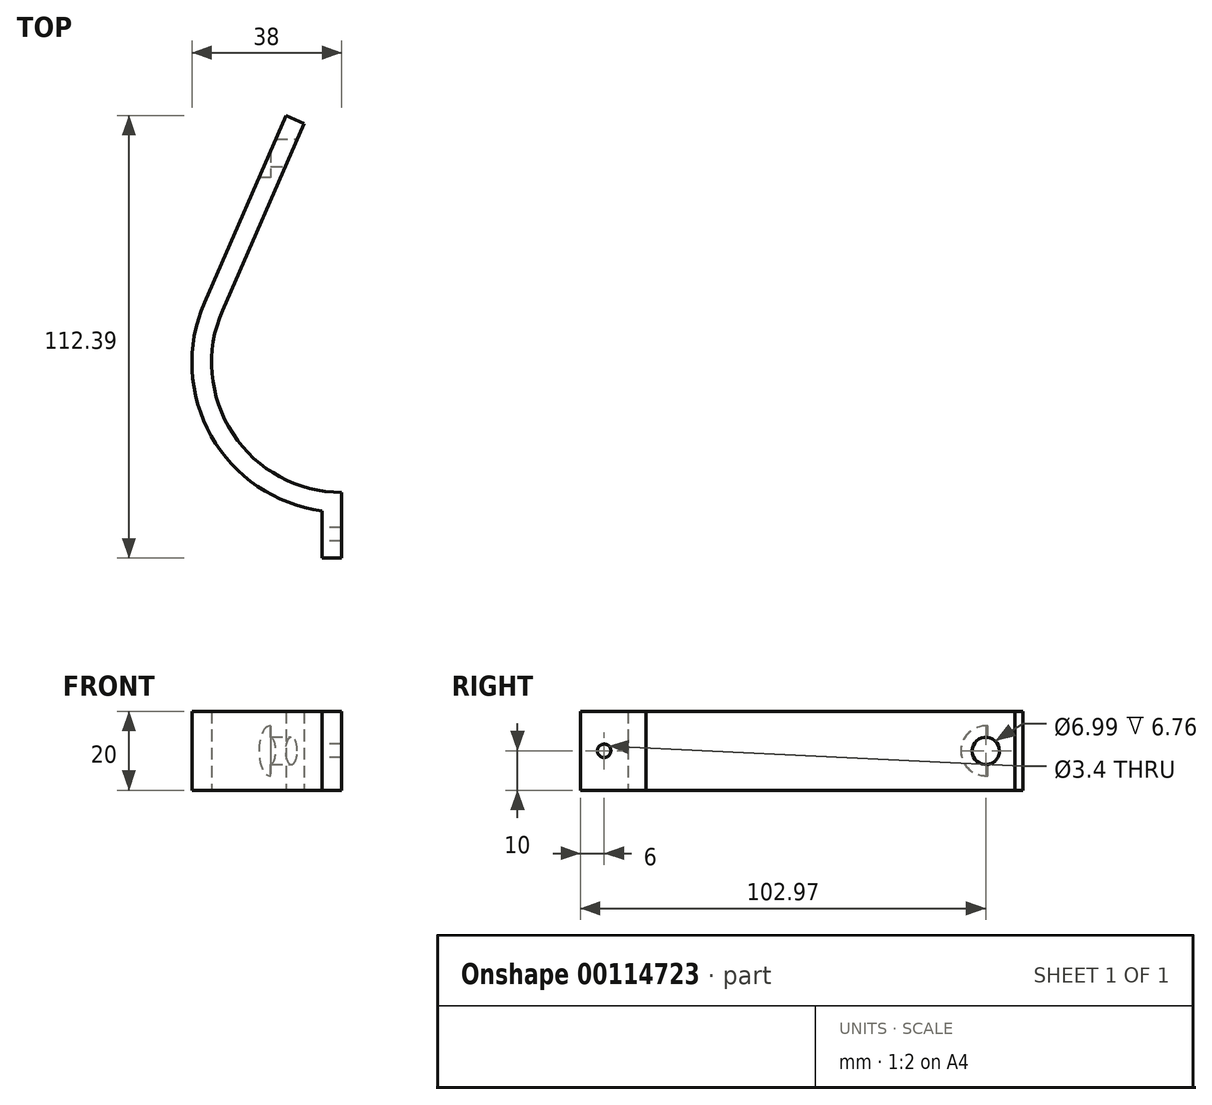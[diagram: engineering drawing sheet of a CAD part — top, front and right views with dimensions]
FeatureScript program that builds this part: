
annotation { "Feature Type Name" : "Feature", "Feature Type Description" : "" }
export const myFeature = defineFeature(function(context is Context, id is Id, definition is map)
    precondition{}
    {
        {
            var Q0;
            Q0=qCreatedBy(makeId("Top.planeOp"),FACE);
            var sketch = newSketch(context, id + "F0", { "sketchPlane" : qUnion([Q0])});
            skPoint(sketch, "E0", {"position": v(0, 98) * mm});
            skArc(sketch, "E1", {"start": v(10.73, 90.98) * mm, "mid": v(0, 98) * mm, "end": v(-10.73, 90.98) * mm});
            skArc(sketch, "E2", {"start": v(-30.25, 46.19) * mm, "mid": v(0, 0) * mm, "end": v(30.25, 46.19) * mm});
            skLineSegment(sketch, "E3", {"start": v(-10.73, 90.98) * mm, "end": v(-30.25, 46.19) * mm});
            skLineSegment(sketch, "E4", {"start": v(10.73, 90.98) * mm, "end": v(30.25, 46.19) * mm});
            skLineSegment(sketch, "E5.0", {"start": v(-15.3, 92.97) * mm, "end": v(-34.83, 48.19) * mm});
            skArc(sketch, "E5.1", {"start": v(15.3, 92.97) * mm, "mid": v(0, 103) * mm, "end": v(-15.3, 92.97) * mm});
            skLineSegment(sketch, "E5.2", {"start": v(15.3, 92.97) * mm, "end": v(34.83, 48.19) * mm});
            skArc(sketch, "E5.3", {"start": v(-34.83, 48.19) * mm, "mid": v(-33.1, 14.32) * mm, "end": v(-5, -4.67) * mm});
            skLineSegment(sketch, "E6", {"start": v(-5, -4.67) * mm, "end": v(-5, -16.67) * mm});
            skLineSegment(sketch, "E7", {"start": v(-5, -16.67) * mm, "end": v(0, -16.67) * mm});
            skArc(sketch, "E8.trimOffspring", {"start": v(0, -5) * mm, "mid": v(31.79, 12.18) * mm, "end": v(34.83, 48.19) * mm});
            skLineSegment(sketch, "E9", {"start": v(0, -5) * mm, "end": v(0, -16.67) * mm});
            skCircle(sketch, "E10", {"center": v(0, 86.3) * mm, "radius": 11.7 * mm, "construction": true});
            skSolve(sketch);
        }
        {
            var Q0;
            Q0=makeQuery(id+"F0.imprint","IMPRINT",FACE,{"disambiguationData":[TD([[makeQuery(id+"F0.imprint","IMPRINT",EDGE,{"derivedFrom":sQuery(id+"F0.wireOp",EDGE,"E1")}),-1.0]])]});
            extrude(context, id + "F1", {"entities" : qUnion([Q0]), "depth" : 20 * mm});
        }
        {
            var Q0;
            Q0=qCreatedBy(makeId("Right.planeOp"),FACE);
            var sketch = newSketch(context, id + "F2", { "sketchPlane" : qUnion([Q0])});
            skPoint(sketch, "E11.0", {"position": v(86.3, 0) * mm});
            skLineSegment(sketch, "E12", {"start": v(86.3, 0) * mm, "end": v(86.3, 10) * mm, "construction": true});
            skCircle(sketch, "E13", {"center": v(86.3, 10) * mm, "radius": 3.5 * mm});
            skSolve(sketch);
        }
        {
            var Q0;
            Q0=makeQuery(id+"F2.imprint","IMPRINT",FACE,{"disambiguationData":[TD([[makeQuery(id+"F2.imprint","IMPRINT",EDGE,{"derivedFrom":sQuery(id+"F2.wireOp",EDGE,"E13")}),1.0]])]});
            extrude(context, id + "F3", {"entities" : qUnion([Q0]), "operationType" : NewBodyOperationType.REMOVE, "endBound" : BoundingType.SYMMETRIC, "oppositeDirection" : true, "depth" : 100 * mm});
        }
        {
            var Q0;
            Q0=qCreatedBy(makeId("Right.planeOp"),FACE);
            cPlane(context, id + "F4", {"entities" : qUnion([Q0]), "cplaneType" : CPlaneType.OFFSET, "offset" : 25 * mm, "oppositeDirection" : true, "width" : 150 * mm, "height" : 150 * mm});
        }
        {
            var Q0;
            Q0=qCreatedBy(id+"F4.planeOp",FACE);
            var sketch = newSketch(context, id + "F5", { "sketchPlane" : qUnion([Q0])});
            skCircle(sketch, "E14.0", {"center": v(86.3, 10) * mm, "radius": 3.5 * mm});
            skCircle(sketch, "E15", {"center": v(86.3, 10) * mm, "radius": 6.35 * mm});
            skSolve(sketch);
        }
        {
            var Q0;
            Q0 = qSketchRegion(id + "F5", true);
            extrude(context, id + "F6", {"entities" : qUnion([Q0]), "operationType" : NewBodyOperationType.REMOVE, "depth" : 7 * mm});
        }
        {
            var Q0;
            Q0=makeQuery(id+"F1.opExtrude","CAP_FACE",FACE,{"disambiguationData":[OSD([sQuery(id+"F0.wireOp",EDGE,"E1"),sQuery(id+"F0.wireOp",EDGE,"E2"),sQuery(id+"F0.wireOp",EDGE,"E3"),sQuery(id+"F0.wireOp",EDGE,"E4"),sQuery(id+"F0.wireOp",EDGE,"E5.0"),sQuery(id+"F0.wireOp",EDGE,"E5.1"),sQuery(id+"F0.wireOp",EDGE,"E5.2"),sQuery(id+"F0.wireOp",EDGE,"E5.3"),sQuery(id+"F0.wireOp",EDGE,"E6"),sQuery(id+"F0.wireOp",EDGE,"E7"),sQuery(id+"F0.wireOp",EDGE,"E8.trimOffspring"),sQuery(id+"F0.wireOp",EDGE,"E9")])],"isStart":false});
            var sketch = newSketch(context, id + "F7", { "sketchPlane" : qUnion([Q0])});
            skPoint(sketch, "E16.firstSnap0", {"position": v(0, 103) * mm});
            skLineSegment(sketch, "E16.bottom", {"start": v(0, -28.68) * mm, "end": v(56.6, -28.68) * mm});
            skLineSegment(sketch, "E16.top", {"start": v(0, 106.36) * mm, "end": v(56.6, 106.36) * mm});
            skLineSegment(sketch, "E16.left", {"start": v(0, -28.68) * mm, "end": v(0, 106.36) * mm});
            skLineSegment(sketch, "E16.right", {"start": v(56.6, -28.68) * mm, "end": v(56.6, 106.36) * mm});
            skSolve(sketch);
        }
        {
            var Q0;
            Q0 = qSketchRegion(id + "F7", true);
            extrude(context, id + "F8", {"entities" : qUnion([Q0]), "operationType" : NewBodyOperationType.REMOVE, "oppositeDirection" : true, "depth" : 25 * mm});
        }
        {
            var Q0;
            Q0=makeQuery(id+"F1.opExtrude","SWEPT_FACE",FACE,{"disambiguationData":[OSD([sQuery(id+"F0.wireOp",EDGE,"E6")])]});
            var sketch = newSketch(context, id + "F9", { "sketchPlane" : qUnion([Q0])});
            skLineSegment(sketch, "E17", {"start": v(10.67, 20) * mm, "end": v(10.67, 0) * mm, "construction": true});
            skCircle(sketch, "E18", {"center": v(10.67, 10) * mm, "radius": 1.7 * mm});
            skSolve(sketch);
        }
        {
            var Q0;
            Q0=makeQuery(id+"F9.imprint","IMPRINT",FACE,{"disambiguationData":[TD([[makeQuery(id+"F9.imprint","IMPRINT",EDGE,{"derivedFrom":sQuery(id+"F9.wireOp",EDGE,"E18")}),1.0]])]});
            extrude(context, id + "F10", {"entities" : qUnion([Q0]), "operationType" : NewBodyOperationType.REMOVE, "oppositeDirection" : true, "depth" : 25 * mm});
        }
        {
            var Q0;
            Q0=makeQuery(id+"F1.opExtrude","CAP_FACE",FACE,{"disambiguationData":[OSD([sQuery(id+"F0.wireOp",EDGE,"E1"),sQuery(id+"F0.wireOp",EDGE,"E2"),sQuery(id+"F0.wireOp",EDGE,"E3"),sQuery(id+"F0.wireOp",EDGE,"E4"),sQuery(id+"F0.wireOp",EDGE,"E5.0"),sQuery(id+"F0.wireOp",EDGE,"E5.1"),sQuery(id+"F0.wireOp",EDGE,"E5.2"),sQuery(id+"F0.wireOp",EDGE,"E5.3"),sQuery(id+"F0.wireOp",EDGE,"E6"),sQuery(id+"F0.wireOp",EDGE,"E7"),sQuery(id+"F0.wireOp",EDGE,"E8.trimOffspring"),sQuery(id+"F0.wireOp",EDGE,"E9")])],"isStart":false});
            var sketch = newSketch(context, id + "F11", { "sketchPlane" : qUnion([Q0])});
            skLineSegment(sketch, "E19", {"start": v(-15.3, 92.97) * mm, "end": v(-10.73, 90.98) * mm});
            skLineSegment(sketch, "E20", {"start": v(-10.73, 90.98) * mm, "end": v(6.22, 97.3) * mm});
            skLineSegment(sketch, "E21", {"start": v(6.22, 97.3) * mm, "end": v(0, 104.07) * mm});
            skLineSegment(sketch, "E22", {"start": v(0, 104.07) * mm, "end": v(-17.91, 98.92) * mm});
            skLineSegment(sketch, "E23", {"start": v(-17.91, 98.92) * mm, "end": v(-15.3, 92.97) * mm});
            skSolve(sketch);
        }
        {
            var Q0;
            Q0 = qSketchRegion(id + "F11", true);
            extrude(context, id + "F12", {"entities" : qUnion([Q0]), "operationType" : NewBodyOperationType.REMOVE, "oppositeDirection" : true, "depth" : 25 * mm});
        }
        {
            var Q0;
            Q0=qCreatedBy(makeId("Top.planeOp"),FACE);
            var sketch = newSketch(context, id + "F13", { "sketchPlane" : qUnion([Q0])});
            skLineSegment(sketch, "E24.0", {"start": v(-15.3, 92.97) * mm, "end": v(-10.73, 90.98) * mm});
            skLineSegment(sketch, "E25", {"start": v(-15.3, 92.97) * mm, "end": v(-14.1, 95.72) * mm});
            skLineSegment(sketch, "E26", {"start": v(-10.73, 90.98) * mm, "end": v(-9.53, 93.73) * mm});
            skLineSegment(sketch, "E27", {"start": v(-14.1, 95.72) * mm, "end": v(-9.53, 93.73) * mm});
            skSolve(sketch);
        }
        {
            var Q0;
            Q0 = qSketchRegion(id + "F13", true);
            extrude(context, id + "F14", {"entities" : qUnion([Q0]), "operationType" : NewBodyOperationType.ADD, "depth" : 20 * mm});
        }
    });
